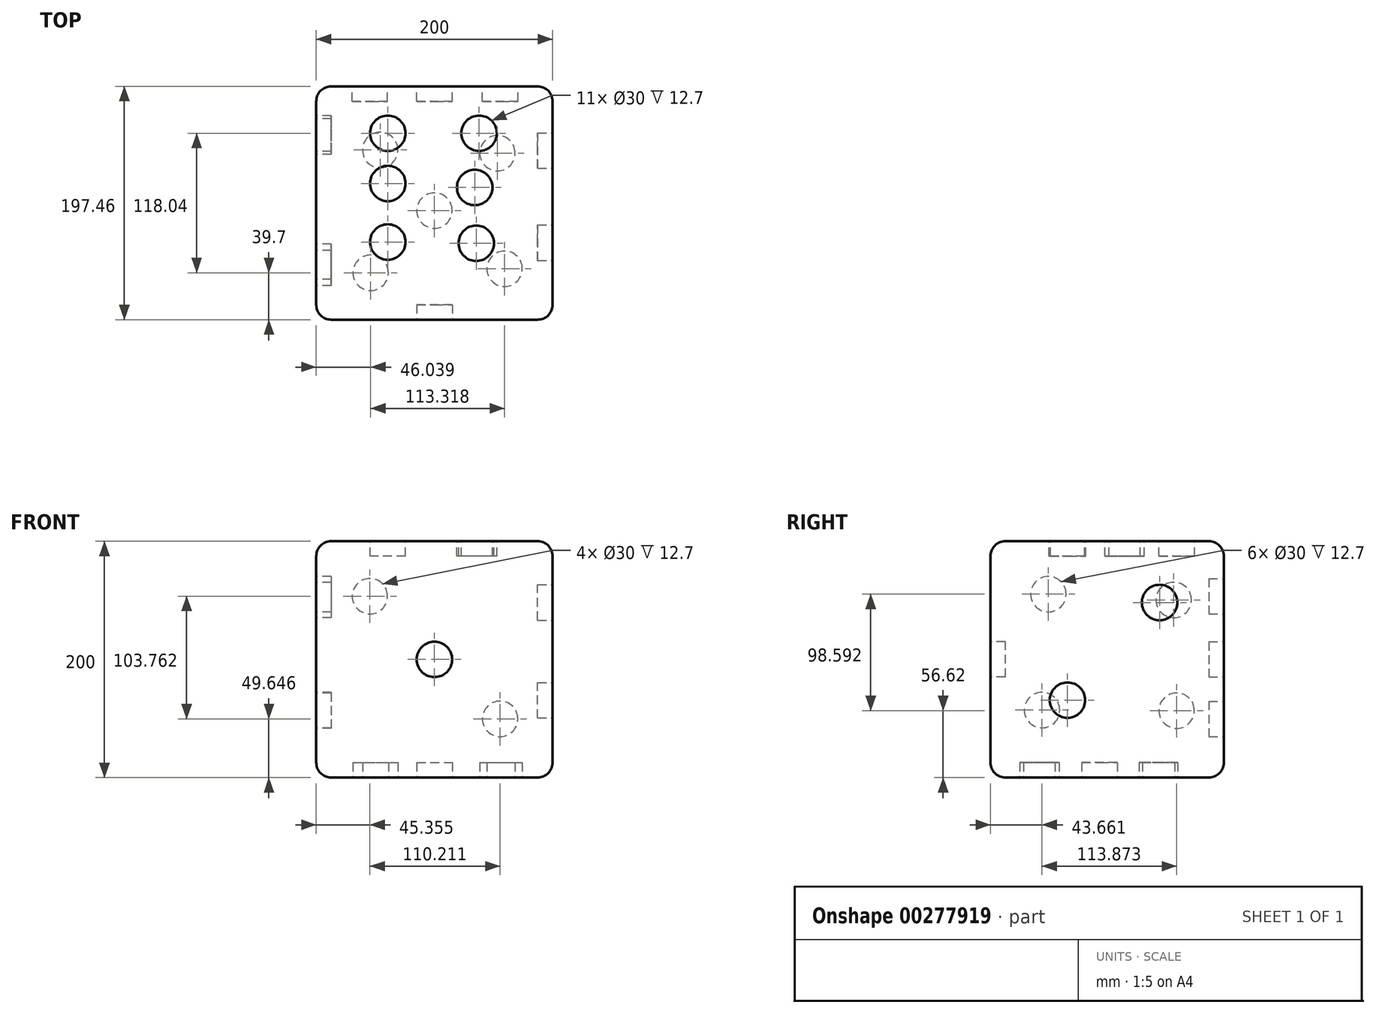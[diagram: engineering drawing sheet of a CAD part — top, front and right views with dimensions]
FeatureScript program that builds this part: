
annotation { "Feature Type Name" : "Feature", "Feature Type Description" : "" }
export const myFeature = defineFeature(function(context is Context, id is Id, definition is map)
    precondition{}
    {
        {
            var Q0;
            Q0=qCreatedBy(makeId("Front.planeOp"),FACE);
            var sketch = newSketch(context, id + "F0", { "sketchPlane" : qUnion([Q0])});
            skLineSegment(sketch, "E0.bottom", {"start": v(100, -100) * mm, "end": v(-100, -100) * mm});
            skLineSegment(sketch, "E0.top", {"start": v(100, 100) * mm, "end": v(-100, 100) * mm});
            skLineSegment(sketch, "E0.left", {"start": v(100, -100) * mm, "end": v(100, 100) * mm});
            skLineSegment(sketch, "E0.right", {"start": v(-100, -100) * mm, "end": v(-100, 100) * mm});
            skPoint(sketch, "E0.middle", {"position": v(0, 0) * mm});
            skSolve(sketch);
        }
        {
            var Q0;
            Q0 = qSketchRegion(id + "F0", true);
            extrude(context, id + "F1", {"entities" : qUnion([Q0]), "depth" : 197.46 * mm});
        }
        {
            var Q0;
            Q0=makeQuery(id+"F1.opExtrude","SWEPT_FACE",FACE,{"disambiguationData":[OSD([sQuery(id+"F0.wireOp",EDGE,"E0.left")])]});
            var Q1;
            Q1=makeQuery(id+"F1.opExtrude","SWEPT_FACE",FACE,{"disambiguationData":[OSD([sQuery(id+"F0.wireOp",EDGE,"E0.top")])]});
            var Q2;
            Q2=makeQuery(id+"F1.opExtrude","CAP_FACE",FACE,{"disambiguationData":[OSD([sQuery(id+"F0.wireOp",EDGE,"E0.bottom"),sQuery(id+"F0.wireOp",EDGE,"E0.top"),sQuery(id+"F0.wireOp",EDGE,"E0.left"),sQuery(id+"F0.wireOp",EDGE,"E0.right")])],"isStart":true});
            var Q3;
            Q3=makeQuery(id+"F1.opExtrude","SWEPT_FACE",FACE,{"disambiguationData":[OSD([sQuery(id+"F0.wireOp",EDGE,"E0.bottom")])]});
            var Q4;
            Q4=makeQuery(id+"F1.opExtrude","SWEPT_FACE",FACE,{"disambiguationData":[OSD([sQuery(id+"F0.wireOp",EDGE,"E0.right")])]});
            var Q5;
            Q5=makeQuery(id+"F1.opExtrude","CAP_FACE",FACE,{"disambiguationData":[OSD([sQuery(id+"F0.wireOp",EDGE,"E0.bottom"),sQuery(id+"F0.wireOp",EDGE,"E0.top"),sQuery(id+"F0.wireOp",EDGE,"E0.left"),sQuery(id+"F0.wireOp",EDGE,"E0.right")])],"isStart":false});
            fillet(context, id + "F2", {"entities" : qUnion([Q0, Q1, Q2, Q3, Q4, Q5]), "radius" : 12.7 * mm, "tangentPropagation" : true, "allowEdgeOverflow" : false});
        }
        {
            var Q0;
            Q0=makeQuery(id+"F1.opExtrude","CAP_FACE",FACE,{"disambiguationData":[OSD([sQuery(id+"F0.wireOp",EDGE,"E0.bottom"),sQuery(id+"F0.wireOp",EDGE,"E0.top"),sQuery(id+"F0.wireOp",EDGE,"E0.left"),sQuery(id+"F0.wireOp",EDGE,"E0.right")])],"isStart":false});
            var sketch = newSketch(context, id + "F3", { "sketchPlane" : qUnion([Q0])});
            skCircle(sketch, "E1", {"center": v(0, 0) * mm, "radius": 15 * mm});
            skSolve(sketch);
        }
        {
            var Q0;
            Q0 = qSketchRegion(id + "F3", true);
            var Q1;
            Q1 = qSketchRegion(id + "F5", true);
            extrude(context, id + "F4", {"entities" : qUnion([Q0, Q1]), "operationType" : NewBodyOperationType.REMOVE, "oppositeDirection" : true, "depth" : 12.7 * mm});
        }
        {
            var Q0;
            Q0=makeQuery(id+"F1.opExtrude","SWEPT_FACE",FACE,{"disambiguationData":[OSD([sQuery(id+"F0.wireOp",EDGE,"E0.left")])]});
            var sketch = newSketch(context, id + "F5", { "sketchPlane" : qUnion([Q0])});
            skCircle(sketch, "E2", {"center": v(-54.31, 48.13) * mm, "radius": 15 * mm});
            skCircle(sketch, "E3", {"center": v(-132.28, -34.53) * mm, "radius": 15 * mm});
            skCircle(sketch, "E4", {"center": v(-245.48, -13.06) * mm, "radius": 3.52 * mm});
            skCircle(sketch, "E5", {"center": v(-271.92, 11.43) * mm, "radius": 2.27 * mm});
            skSolve(sketch);
        }
        {
            var Q0;
            Q0=makeQuery(id+"F1.opExtrude","CAP_FACE",FACE,{"disambiguationData":[OSD([sQuery(id+"F0.wireOp",EDGE,"E0.bottom"),sQuery(id+"F0.wireOp",EDGE,"E0.top"),sQuery(id+"F0.wireOp",EDGE,"E0.left"),sQuery(id+"F0.wireOp",EDGE,"E0.right")])],"isStart":true});
            var sketch = newSketch(context, id + "F6", { "sketchPlane" : qUnion([Q0])});
            skCircle(sketch, "E6", {"center": v(54.65, 53.4) * mm, "radius": 15 * mm});
            skCircle(sketch, "E7", {"center": v(0, 0) * mm, "radius": 15 * mm});
            skCircle(sketch, "E8", {"center": v(-55.57, -50.35) * mm, "radius": 15 * mm});
            skSolve(sketch);
        }
        {
            var Q0;
            Q0=makeQuery(id+"F6.imprint","IMPRINT",FACE,{"disambiguationData":[TD([[makeQuery(id+"F6.imprint","IMPRINT",EDGE,{"derivedFrom":sQuery(id+"F6.wireOp",EDGE,"E6")}),1.0]])]});
            var Q1;
            Q1=makeQuery(id+"F6.imprint","IMPRINT",FACE,{"disambiguationData":[TD([[makeQuery(id+"F6.imprint","IMPRINT",EDGE,{"derivedFrom":sQuery(id+"F6.wireOp",EDGE,"E7")}),1.0]])]});
            var Q2;
            Q2=makeQuery(id+"F6.imprint","IMPRINT",FACE,{"disambiguationData":[TD([[makeQuery(id+"F6.imprint","IMPRINT",EDGE,{"derivedFrom":sQuery(id+"F6.wireOp",EDGE,"E8")}),1.0]])]});
            var Q3;
            Q3=sQuery(id+"F6.wireOp",EDGE,"E6");
            extrude(context, id + "F7", {"entities" : qUnion([Q0, Q1, Q2]), "operationType" : NewBodyOperationType.REMOVE, "surfaceEntities" : qUnion([Q3]), "oppositeDirection" : true, "depth" : 12.7 * mm});
        }
        {
            var Q0;
            Q0=makeQuery(id+"F5.imprint","IMPRINT",FACE,{"disambiguationData":[TD([[makeQuery(id+"F5.imprint","IMPRINT",EDGE,{"derivedFrom":sQuery(id+"F5.wireOp",EDGE,"E3")}),1.0]])]});
            var Q1;
            Q1=makeQuery(id+"F5.imprint","IMPRINT",FACE,{"disambiguationData":[TD([[makeQuery(id+"F5.imprint","IMPRINT",EDGE,{"derivedFrom":sQuery(id+"F5.wireOp",EDGE,"E2")}),1.0]])]});
            extrude(context, id + "F8", {"entities" : qUnion([Q0, Q1]), "operationType" : NewBodyOperationType.REMOVE, "oppositeDirection" : true, "depth" : 12.7 * mm});
        }
        {
            var Q0;
            Q0=makeQuery(id+"F1.opExtrude","SWEPT_FACE",FACE,{"disambiguationData":[OSD([sQuery(id+"F0.wireOp",EDGE,"E0.right")])]});
            var sketch = newSketch(context, id + "F9", { "sketchPlane" : qUnion([Q0])});
            skCircle(sketch, "E9", {"center": v(42.4, 50.28) * mm, "radius": 15 * mm});
            skCircle(sketch, "E10", {"center": v(148.38, 55.21) * mm, "radius": 15 * mm});
            skCircle(sketch, "E11", {"center": v(39.93, -43.38) * mm, "radius": 15 * mm});
            skCircle(sketch, "E12", {"center": v(153.8, -42.89) * mm, "radius": 15 * mm});
            skSolve(sketch);
        }
        {
            var Q0;
            Q0=makeQuery(id+"F9.imprint","IMPRINT",FACE,{"disambiguationData":[TD([[makeQuery(id+"F9.imprint","IMPRINT",EDGE,{"derivedFrom":sQuery(id+"F9.wireOp",EDGE,"E9")}),1.0]])]});
            var Q1;
            Q1=makeQuery(id+"F9.imprint","IMPRINT",FACE,{"disambiguationData":[TD([[makeQuery(id+"F9.imprint","IMPRINT",EDGE,{"derivedFrom":sQuery(id+"F9.wireOp",EDGE,"E11")}),1.0]])]});
            var Q2;
            Q2=makeQuery(id+"F9.imprint","IMPRINT",FACE,{"disambiguationData":[TD([[makeQuery(id+"F9.imprint","IMPRINT",EDGE,{"derivedFrom":sQuery(id+"F9.wireOp",EDGE,"E10")}),1.0]])]});
            var Q3;
            Q3=makeQuery(id+"F9.imprint","IMPRINT",FACE,{"disambiguationData":[TD([[makeQuery(id+"F9.imprint","IMPRINT",EDGE,{"derivedFrom":sQuery(id+"F9.wireOp",EDGE,"E12")}),1.0]])]});
            extrude(context, id + "F10", {"entities" : qUnion([Q0, Q1, Q2, Q3]), "operationType" : NewBodyOperationType.REMOVE, "oppositeDirection" : true, "depth" : 12.7 * mm});
        }
        {
            var Q0;
            Q0=makeQuery(id+"F1.opExtrude","SWEPT_FACE",FACE,{"disambiguationData":[OSD([sQuery(id+"F0.wireOp",EDGE,"E0.bottom")])]});
            var sketch = newSketch(context, id + "F11", { "sketchPlane" : qUnion([Q0])});
            skCircle(sketch, "E13", {"center": v(-53.96, 157.76) * mm, "radius": 15 * mm});
            skCircle(sketch, "E14", {"center": v(59.36, 154.39) * mm, "radius": 15 * mm});
            skCircle(sketch, "E15", {"center": v(0, 105.15) * mm, "radius": 15 * mm});
            skCircle(sketch, "E16", {"center": v(-45.87, 53.88) * mm, "radius": 15 * mm});
            skCircle(sketch, "E17", {"center": v(53.29, 56.58) * mm, "radius": 15 * mm});
            skSolve(sketch);
        }
        {
            var Q0;
            Q0=makeQuery(id+"F11.imprint","IMPRINT",FACE,{"disambiguationData":[TD([[makeQuery(id+"F11.imprint","IMPRINT",EDGE,{"derivedFrom":sQuery(id+"F11.wireOp",EDGE,"E15")}),1.0]])]});
            var Q1;
            Q1=makeQuery(id+"F11.imprint","IMPRINT",FACE,{"disambiguationData":[TD([[makeQuery(id+"F11.imprint","IMPRINT",EDGE,{"derivedFrom":sQuery(id+"F11.wireOp",EDGE,"E17")}),1.0]])]});
            var Q2;
            Q2=makeQuery(id+"F11.imprint","IMPRINT",FACE,{"disambiguationData":[TD([[makeQuery(id+"F11.imprint","IMPRINT",EDGE,{"derivedFrom":sQuery(id+"F11.wireOp",EDGE,"E16")}),1.0]])]});
            var Q3;
            Q3=makeQuery(id+"F11.imprint","IMPRINT",FACE,{"disambiguationData":[TD([[makeQuery(id+"F11.imprint","IMPRINT",EDGE,{"derivedFrom":sQuery(id+"F11.wireOp",EDGE,"E13")}),1.0]])]});
            var Q4;
            Q4=makeQuery(id+"F11.imprint","IMPRINT",FACE,{"disambiguationData":[TD([[makeQuery(id+"F11.imprint","IMPRINT",EDGE,{"derivedFrom":sQuery(id+"F11.wireOp",EDGE,"E14")}),1.0]])]});
            extrude(context, id + "F12", {"entities" : qUnion([Q0, Q1, Q2, Q3, Q4]), "operationType" : NewBodyOperationType.REMOVE, "oppositeDirection" : true, "depth" : 12.7 * mm});
        }
        {
            var Q0;
            Q0=makeQuery(id+"F1.opExtrude","SWEPT_FACE",FACE,{"disambiguationData":[OSD([sQuery(id+"F0.wireOp",EDGE,"E0.top")])]});
            var sketch = newSketch(context, id + "F13", { "sketchPlane" : qUnion([Q0])});
            skCircle(sketch, "E18", {"center": v(-39.46, -39.72) * mm, "radius": 15 * mm});
            skCircle(sketch, "E19", {"center": v(-39.46, -82.21) * mm, "radius": 15 * mm});
            skCircle(sketch, "E20", {"center": v(-39.46, -131.74) * mm, "radius": 15 * mm});
            skCircle(sketch, "E21", {"center": v(37.8, -39.72) * mm, "radius": 15 * mm});
            skCircle(sketch, "E22", {"center": v(34.06, -85.59) * mm, "radius": 15 * mm});
            skCircle(sketch, "E23", {"center": v(35.41, -132.8) * mm, "radius": 15 * mm});
            skSolve(sketch);
        }
        {
            var Q0;
            Q0=makeQuery(id+"F13.imprint","IMPRINT",FACE,{"disambiguationData":[TD([[makeQuery(id+"F13.imprint","IMPRINT",EDGE,{"derivedFrom":sQuery(id+"F13.wireOp",EDGE,"E18")}),1.0]])]});
            var Q1;
            Q1=makeQuery(id+"F13.imprint","IMPRINT",FACE,{"disambiguationData":[TD([[makeQuery(id+"F13.imprint","IMPRINT",EDGE,{"derivedFrom":sQuery(id+"F13.wireOp",EDGE,"E21")}),1.0]])]});
            var Q2;
            Q2=makeQuery(id+"F13.imprint","IMPRINT",FACE,{"disambiguationData":[TD([[makeQuery(id+"F13.imprint","IMPRINT",EDGE,{"derivedFrom":sQuery(id+"F13.wireOp",EDGE,"E19")}),1.0]])]});
            var Q3;
            Q3=makeQuery(id+"F13.imprint","IMPRINT",FACE,{"disambiguationData":[TD([[makeQuery(id+"F13.imprint","IMPRINT",EDGE,{"derivedFrom":sQuery(id+"F13.wireOp",EDGE,"E22")}),1.0]])]});
            var Q4;
            Q4=makeQuery(id+"F13.imprint","IMPRINT",FACE,{"disambiguationData":[TD([[makeQuery(id+"F13.imprint","IMPRINT",EDGE,{"derivedFrom":sQuery(id+"F13.wireOp",EDGE,"E20")}),1.0]])]});
            var Q5;
            Q5=makeQuery(id+"F13.imprint","IMPRINT",FACE,{"disambiguationData":[TD([[makeQuery(id+"F13.imprint","IMPRINT",EDGE,{"derivedFrom":sQuery(id+"F13.wireOp",EDGE,"E23")}),1.0]])]});
            extrude(context, id + "F14", {"entities" : qUnion([Q0, Q1, Q2, Q3, Q4, Q5]), "operationType" : NewBodyOperationType.REMOVE, "oppositeDirection" : true, "depth" : 12.7 * mm});
        }
    });
